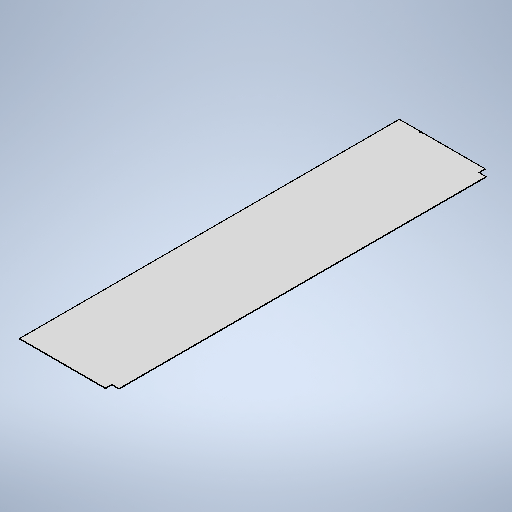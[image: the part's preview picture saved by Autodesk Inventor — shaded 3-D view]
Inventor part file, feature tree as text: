
AUTODESK INVENTOR PART (.ipt)
format: ipt  version: 2025.3 (Build 293356000, 356)  size: 293,376 bytes
history: native  units: mm
features: other x3, sketch x2, sheet_metal_op x1
ambient origin geometry x8: Origin, YZ Plane, XZ Plane, XY Plane, X Axis, Y Axis, Z Axis, Center Point
bodies: Solid1 (feature_tree)
feature tree (6):
  sheet_metal_op  "Face1"
  sketch  "Sketch1"  dims[d2=3.0mm]
  other  "Plate1"
  sketch  "Sketch5"  dims[d22=515.0mm d23=2100.0mm d24=40.0mm d25=35.0mm d28=100.0mm d29=200.0mm d30=100.0mm d31=2.0mm d32=5.0mm d33=4.0mm d34=0.5mm d35=5.0mm d36=5.0mm d37=5.0mm d38=2.0mm d39=3.0mm d40=0.0mm]
  other  "Cut1"
  other  "Definition1"
